# Revit family: Flushometer-High_Efficiency-Sloan-Ecos-8186_Series
name_source: partatom
category: Plumbing Fixtures
revit_build: Autodesk Revit 2014 (Build: 20130308_1515(x64)
units: mm (PartAtom-declared; Revit-internal decimal feet)

## types (3) — shared parameters
ADA Compliant = Yes
Assembly Code = D2020100
Buy American Act Compliant = Yes
CW Connection = Yes
CWFU = 5
Cold Water Connection Radius = 0' - 0 3/8"
Default Elevation = 0' - 0"
Description = Exposed, hardwired, high-efficiency Sloan ECOS® urinal flushometer with Smart Sense Technology™, for high-efficiency top spud urinals.
Finishes = CP, PVDSF, PVDPB, PVDBN
Fixture Color = Not Applicable
Flush Choice = Single Flush
HW Connection = No
High-Efficiency = Yes
IAPMO Certification = cUPC
Inlet Spud Size = 1" IPS
Manufacturer = SLOAN
Material = Metal-Sloan-Chrome Plated
Mounting = Exposed
Operation = Sensor-Activated
Price = Prices may vary. Please consult Sloan Rep for most up-to-date price list.
Product Page URL = https://www.sloan.com
Rough-in = 11-1/2"
Specification Sheet = https://specifications.sloan.com
Spud Location = Top Spud
URL = www.sloanvalve.com
Vent Connection = No
Warranty = 3 Year (Limited)
Waste Connection = No
zero-valued in all types: HWFU, WFU

## per-type parameters (varying)
| type | Flush Rate |
| ECOS 8186-0.5 | 0.5 gpf (1.9 Lpf) |
| ECOS 8186-0.125 | 0.125 gpf (0.5 Lpf) |
| ECOS 8186-0.25 | 0.25 gpf (1.0 Lpf) |

note: column(s) folded — value = type name in every type: Model

## geometry (parser evidence)
native form markers: Sweep x1
no freeform markers — native parametric forms only
